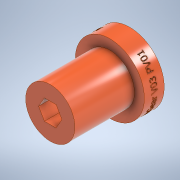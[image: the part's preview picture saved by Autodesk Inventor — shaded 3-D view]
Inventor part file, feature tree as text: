
AUTODESK INVENTOR PART (.ipt)
format: ipt  version: 2022.2 (Build 262287010, 287A)  size: 1,906,176 bytes
history: native  units: in
note: dims shown in document units (in); Inventor stores cm internally (conversion verified against a paired STEP export)
features: sketch x9, extrude x6, hole x2, plane x1, emboss x1
ambient origin geometry x8: Origin, YZ Plane, XZ Plane, XY Plane, X Axis, Y Axis, Z Axis, Center Point
bodies: Solid1 (feature_tree)
feature tree (19):
  extrude  "Extrusion1"  Depth=0.5in TaperAngle=0.0deg
  extrude  "Extrusion2"  Depth=0.75in TaperAngle=0.0deg
  extrude  "Base"  Depth=0.5in TaperAngle=0.0deg
  hole  "Hole1"  [1 undecoded]
  hole  "Hole2"  [1 undecoded]
  plane  "Work Plane1"
  emboss  "Emboss2"
  extrude  "Extrusion4"  Depth=0.75in TaperAngle=0.0deg
  extrude  "Extrusion5"  [1 undecoded]
  extrude  "Extrusion6"  [1 undecoded]
  sketch  "Sketch1"  dims[d0=0.5in d1=1.0in d2=0.0in]
  sketch  "Sketch2"  dims[d3=1.24in d4=0.75in d5=0.0in]
  sketch  "Sketch3"  dims[d6=1.74in d7=0.5in d8=0.0in]
  sketch  "Sketch6"  dims[d13=0.244in]
  sketch  "Sketch7"  dims[d14=0.17in d15=0.75in d16=0.5in d17=0.093in d18=0.5635in d19=1.0in d20=0.8108in]
  sketch  "Sketch8"  dims[d21=0.249in d22=0.75in d23=0.26in d24=0.2411in d25=0.5635in d26=0.31in d27=0.0in d28=0.1in d29=0.0in]
  sketch  "Sketch9"  dims[d30=1.0in d31=0.0in d32=0.51in]
  sketch  "Sketch10"  dims[d33=0.0in d34=0.0in d35=0.75in d36=0.0in]
  sketch  "Sketch11"
note: 4 required parameter values undecoded (feature->parameter linkage not recoverable at this tier; creation-order binding heuristic only, values carry confidence <= 0.55)
